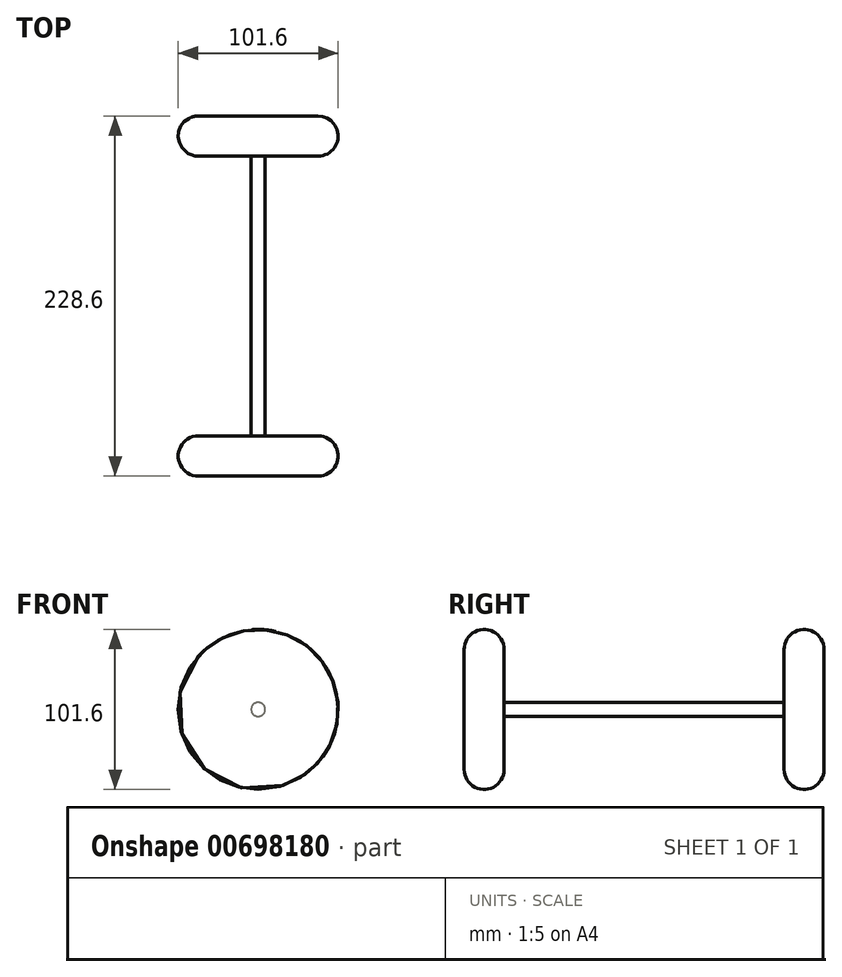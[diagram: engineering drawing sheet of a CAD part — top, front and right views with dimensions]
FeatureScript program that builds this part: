
annotation { "Feature Type Name" : "Feature", "Feature Type Description" : "" }
export const myFeature = defineFeature(function(context is Context, id is Id, definition is map)
    precondition{}
    {
        {
            var Q0;
            Q0=qCreatedBy(makeId("Front.planeOp"),FACE);
            var sketch = newSketch(context, id + "F0", { "sketchPlane" : qUnion([Q0])});
            skCircle(sketch, "E0", {"center": v(0, 0) * mm, "radius": 50.8 * mm});
            skSolve(sketch);
        }
        {
            var Q0;
            Q0 = qSketchRegion(id + "F0", true);
            extrude(context, id + "F1", {"entities" : qUnion([Q0]), "depth" : 25.4 * mm, "offsetDistance" : 25.4 * mm});
        }
        {
            var Q0;
            Q0=makeQuery(id+"F1.opExtrude","CAP_EDGE",EDGE,{"disambiguationData":[OSD([sQuery(id+"F0.wireOp",EDGE,"E0")])],"isStart":false});
            fillet(context, id + "F2", {"entities" : qUnion([Q0]), "radius" : 12.7 * mm, "tangentPropagation" : true, "allowEdgeOverflow" : false});
        }
        {
            var Q0;
            Q0=makeQuery(id+"F1.opExtrude","SWEPT_FACE",FACE,{"disambiguationData":[OSD([sQuery(id+"F0.wireOp",EDGE,"E0")])]});
            fillet(context, id + "F3", {"entities" : qUnion([Q0]), "radius" : 12.7 * mm, "tangentPropagation" : true, "allowEdgeOverflow" : false});
        }
        {
            var Q0;
            Q0=makeQuery(id+"F1.opExtrude","CAP_FACE",FACE,{"disambiguationData":[OSD([sQuery(id+"F0.wireOp",EDGE,"E0")])],"isStart":true});
            var sketch = newSketch(context, id + "F4", { "sketchPlane" : qUnion([Q0])});
            skCircle(sketch, "E1", {"center": v(0, 0) * mm, "radius": 4.45 * mm});
            skSolve(sketch);
        }
        {
            var Q0;
            Q0=makeQuery(id+"F4.imprint","IMPRINT",FACE,{"disambiguationData":[TD([[makeQuery(id+"F4.imprint","IMPRINT",EDGE,{"derivedFrom":sQuery(id+"F4.wireOp",EDGE,"E1")}),1.0]])]});
            extrude(context, id + "F5", {"entities" : qUnion([Q0]), "operationType" : NewBodyOperationType.ADD, "depth" : 177.8 * mm, "offsetDistance" : 25.4 * mm});
        }
        {
            var Q0;
            Q0=makeQuery(id+"F5.opExtrude","CAP_FACE",FACE,{"disambiguationData":[OSD([sQuery(id+"F4.wireOp",EDGE,"E1")])],"isStart":false});
            var sketch = newSketch(context, id + "F6", { "sketchPlane" : qUnion([Q0])});
            skCircle(sketch, "E2", {"center": v(0, 0) * mm, "radius": 50.8 * mm});
            skSolve(sketch);
        }
        {
            var Q0;
            Q0 = qSketchRegion(id + "F6", true);
            extrude(context, id + "F7", {"entities" : qUnion([Q0]), "operationType" : NewBodyOperationType.ADD, "depth" : 25.4 * mm, "offsetDistance" : 25.4 * mm});
        }
        {
            var Q0;
            Q0=makeQuery(id+"F7.opExtrude","CAP_EDGE",EDGE,{"disambiguationData":[OSD([sQuery(id+"F6.wireOp",EDGE,"E2")])],"isStart":true});
            fillet(context, id + "F8", {"entities" : qUnion([Q0]), "radius" : 12.7 * mm, "tangentPropagation" : true, "allowEdgeOverflow" : false});
        }
        {
            var Q0;
            Q0=makeQuery(id+"F7.opExtrude","CAP_EDGE",EDGE,{"disambiguationData":[OSD([sQuery(id+"F6.wireOp",EDGE,"E2")])],"isStart":false});
            fillet(context, id + "F9", {"entities" : qUnion([Q0]), "radius" : 12.7 * mm, "tangentPropagation" : true, "allowEdgeOverflow" : false});
        }
    });
